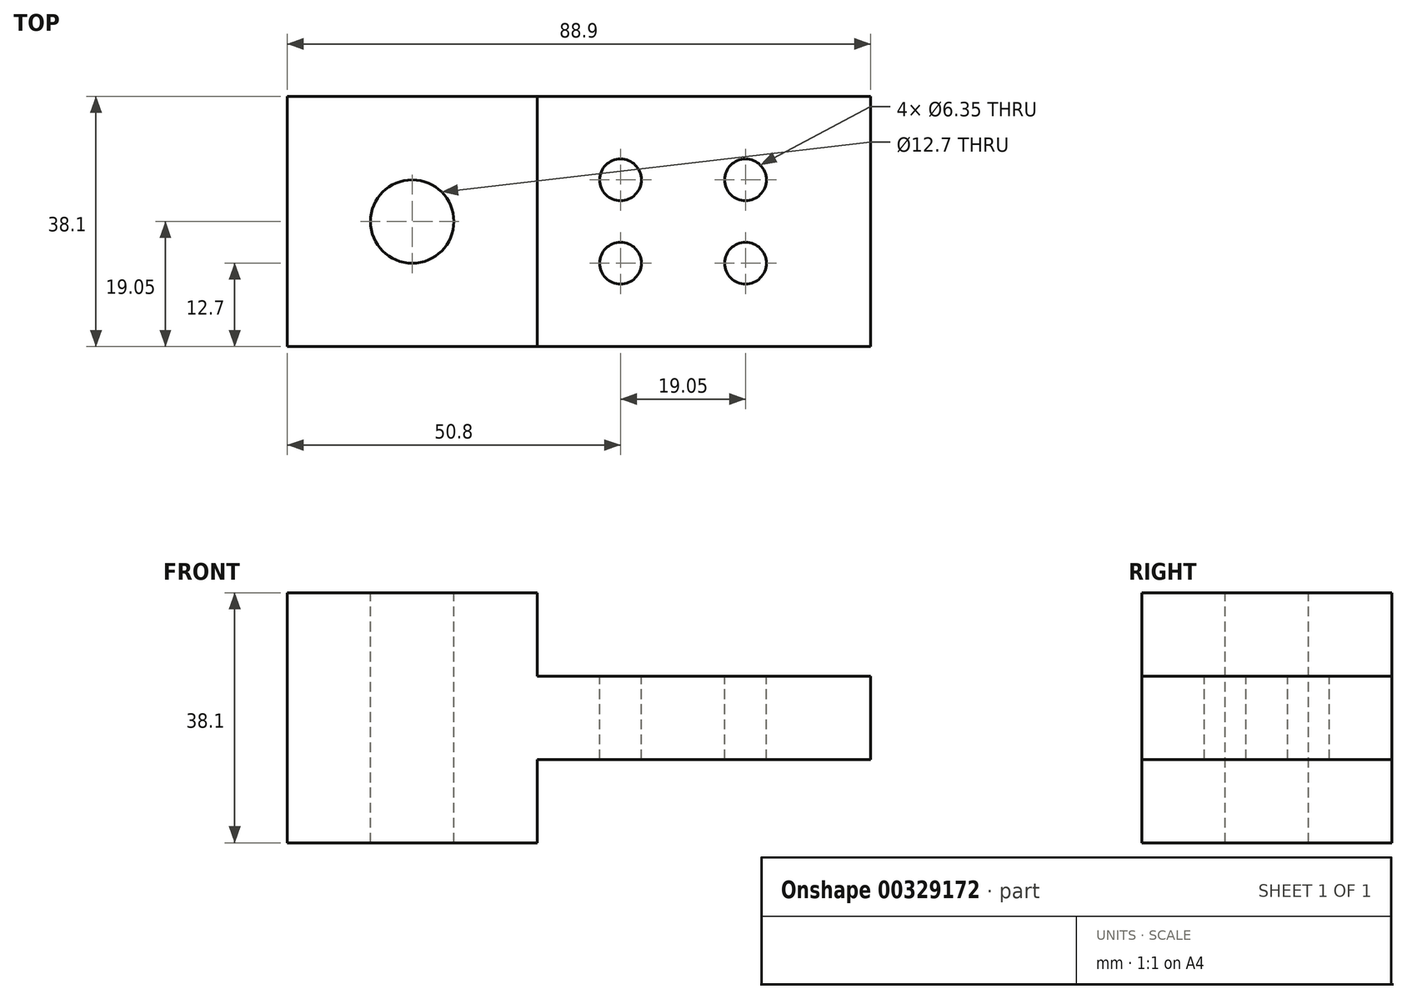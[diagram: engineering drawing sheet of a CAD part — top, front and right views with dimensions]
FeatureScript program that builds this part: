
annotation { "Feature Type Name" : "Feature", "Feature Type Description" : "" }
export const myFeature = defineFeature(function(context is Context, id is Id, definition is map)
    precondition{}
    {
        {
            var Q0;
            Q0=qCreatedBy(makeId("Front.planeOp"),FACE);
            var sketch = newSketch(context, id + "F0", { "sketchPlane" : qUnion([Q0])});
            skLineSegment(sketch, "E0", {"start": v(0, 0) * mm, "end": v(0, 38.1) * mm});
            skLineSegment(sketch, "E1", {"start": v(0, 38.1) * mm, "end": v(38.1, 38.1) * mm});
            skLineSegment(sketch, "E2", {"start": v(38.1, 38.1) * mm, "end": v(38.1, 25.4) * mm});
            skLineSegment(sketch, "E3", {"start": v(38.1, 25.4) * mm, "end": v(88.9, 25.4) * mm});
            skLineSegment(sketch, "E4", {"start": v(88.9, 25.4) * mm, "end": v(88.9, 12.7) * mm});
            skLineSegment(sketch, "E5", {"start": v(88.9, 12.7) * mm, "end": v(38.1, 12.7) * mm});
            skLineSegment(sketch, "E6", {"start": v(38.1, 12.7) * mm, "end": v(38.1, 0) * mm});
            skLineSegment(sketch, "E7", {"start": v(38.1, 0) * mm, "end": v(0, 0) * mm});
            skSolve(sketch);
        }
        {
            var Q0;
            Q0=makeQuery(id+"F0.imprint","IMPRINT",FACE,{"disambiguationData":[TD([[makeQuery(id+"F0.imprint","IMPRINT",EDGE,{"derivedFrom":sQuery(id+"F0.wireOp",EDGE,"E0")}),-1.0]])]});
            extrude(context, id + "F1", {"entities" : qUnion([Q0]), "depth" : 38.1 * mm});
        }
        {
            var Q0;
            Q0=makeQuery(id+"F1.opExtrude","SWEPT_FACE",FACE,{"disambiguationData":[OSD([sQuery(id+"F0.wireOp",EDGE,"E3")])]});
            var sketch = newSketch(context, id + "F2", { "sketchPlane" : qUnion([Q0])});
            skPoint(sketch, "E8.endSnap0", {"position": v(88.9, -19.05) * mm});
            skLineSegment(sketch, "E9", {"start": v(88.9, -19.05) * mm, "end": v(31.39, -19.05) * mm, "construction": true});
            skPoint(sketch, "E9.endSnap0", {"position": v(38.1, -19.05) * mm});
            skArc(sketch, "E10", {"start": v(69.27, 0) * mm, "mid": v(88.9, -19.05) * mm, "end": v(69.27, -38.1) * mm});
            skLineSegment(sketch, "E11", {"start": v(69.27, 0) * mm, "end": v(88.9, 0) * mm});
            skLineSegment(sketch, "E12", {"start": v(88.9, 0) * mm, "end": v(88.9, -38.1) * mm});
            skLineSegment(sketch, "E13", {"start": v(88.9, -38.1) * mm, "end": v(69.27, -38.1) * mm});
            skSolve(sketch);
        }
        {
            var Q0;
            {var subQ0=sQuery(id+"F2.wireOp",EDGE,"E11");var subQ1=sQuery(id+"F2.wireOp",EDGE,"E10");var subQ2=makeQuery(id+"F2.imprint","INTERSECT",VERTEX,{"derivedFrom":[subQ1,subQ0]});Q0=makeQuery(id+"F2.imprint","IMPRINT",FACE,{"disambiguationData":[TD([[makeQuery(id+"F2.imprint","IMPRINT",EDGE,{"disambiguationData":[TD([[subQ2,-1.0]])],"derivedFrom":subQ1}),1.0]])]});}
            extrude(context, id + "F3", {"entities" : qUnion([Q0]), "operationType" : NewBodyOperationType.REMOVE, "endBound" : BoundingType.THROUGH_ALL, "oppositeDirection" : true, "depth" : 25.4 * mm});
        }
        {
            var Q0;
            {var subQ0=sQuery(id+"F2.wireOp",EDGE,"E12");var subQ1=sQuery(id+"F2.wireOp",EDGE,"E10");var subQ2=makeQuery(id+"F2.imprint","INTERSECT",VERTEX,{"disambiguationData":[OD(1.0)],"derivedFrom":[subQ1,subQ0]});Q0=makeQuery(id+"F2.imprint","IMPRINT",FACE,{"disambiguationData":[TD([[makeQuery(id+"F2.imprint","IMPRINT",EDGE,{"disambiguationData":[TD([[subQ2,-1.0]])],"derivedFrom":subQ1}),1.0]])]});}
            extrude(context, id + "F4", {"entities" : qUnion([Q0]), "operationType" : NewBodyOperationType.REMOVE, "endBound" : BoundingType.THROUGH_ALL, "oppositeDirection" : true, "depth" : 25.4 * mm});
        }
        {
            var Q0;
            Q0=makeQuery(id+"F1.opExtrude","SWEPT_FACE",FACE,{"disambiguationData":[OSD([sQuery(id+"F0.wireOp",EDGE,"E1")])]});
            var sketch = newSketch(context, id + "F5", { "sketchPlane" : qUnion([Q0])});
            skCircle(sketch, "E14", {"center": v(19.05, -19.05) * mm, "radius": 6.35 * mm});
            skSolve(sketch);
        }
        {
            var Q0;
            Q0=makeQuery(id+"F5.imprint","IMPRINT",FACE,{"disambiguationData":[TD([[makeQuery(id+"F5.imprint","IMPRINT",EDGE,{"derivedFrom":sQuery(id+"F5.wireOp",EDGE,"E14")}),1.0]])]});
            extrude(context, id + "F6", {"entities" : qUnion([Q0]), "operationType" : NewBodyOperationType.REMOVE, "endBound" : BoundingType.THROUGH_ALL, "oppositeDirection" : true, "depth" : 25.4 * mm});
        }
        {
            var Q0;
            Q0=makeQuery(id+"F1.opExtrude","SWEPT_FACE",FACE,{"disambiguationData":[OSD([sQuery(id+"F0.wireOp",EDGE,"E3")])]});
            var sketch = newSketch(context, id + "F7", { "sketchPlane" : qUnion([Q0])});
            skCircle(sketch, "E15", {"center": v(50.8, -12.7) * mm, "radius": 3.18 * mm});
            skCircle(sketch, "E16", {"center": v(69.85, -12.7) * mm, "radius": 3.18 * mm});
            skCircle(sketch, "E17", {"center": v(50.8, -25.4) * mm, "radius": 3.18 * mm});
            skCircle(sketch, "E18", {"center": v(69.85, -25.4) * mm, "radius": 3.18 * mm});
            skSolve(sketch);
        }
        {
            var Q0;
            Q0=makeQuery(id+"F7.imprint","IMPRINT",FACE,{"disambiguationData":[TD([[makeQuery(id+"F7.imprint","IMPRINT",EDGE,{"derivedFrom":sQuery(id+"F7.wireOp",EDGE,"E15")}),1.0]])]});
            var Q1;
            Q1=makeQuery(id+"F7.imprint","IMPRINT",FACE,{"disambiguationData":[TD([[makeQuery(id+"F7.imprint","IMPRINT",EDGE,{"derivedFrom":sQuery(id+"F7.wireOp",EDGE,"E16")}),1.0]])]});
            var Q2;
            Q2=makeQuery(id+"F7.imprint","IMPRINT",FACE,{"disambiguationData":[TD([[makeQuery(id+"F7.imprint","IMPRINT",EDGE,{"derivedFrom":sQuery(id+"F7.wireOp",EDGE,"E17")}),1.0]])]});
            var Q3;
            Q3=makeQuery(id+"F7.imprint","IMPRINT",FACE,{"disambiguationData":[TD([[makeQuery(id+"F7.imprint","IMPRINT",EDGE,{"derivedFrom":sQuery(id+"F7.wireOp",EDGE,"E18")}),1.0]])]});
            extrude(context, id + "F8", {"entities" : qUnion([Q0, Q1, Q2, Q3]), "operationType" : NewBodyOperationType.REMOVE, "endBound" : BoundingType.THROUGH_ALL, "oppositeDirection" : true, "depth" : 25.4 * mm});
        }
    });
